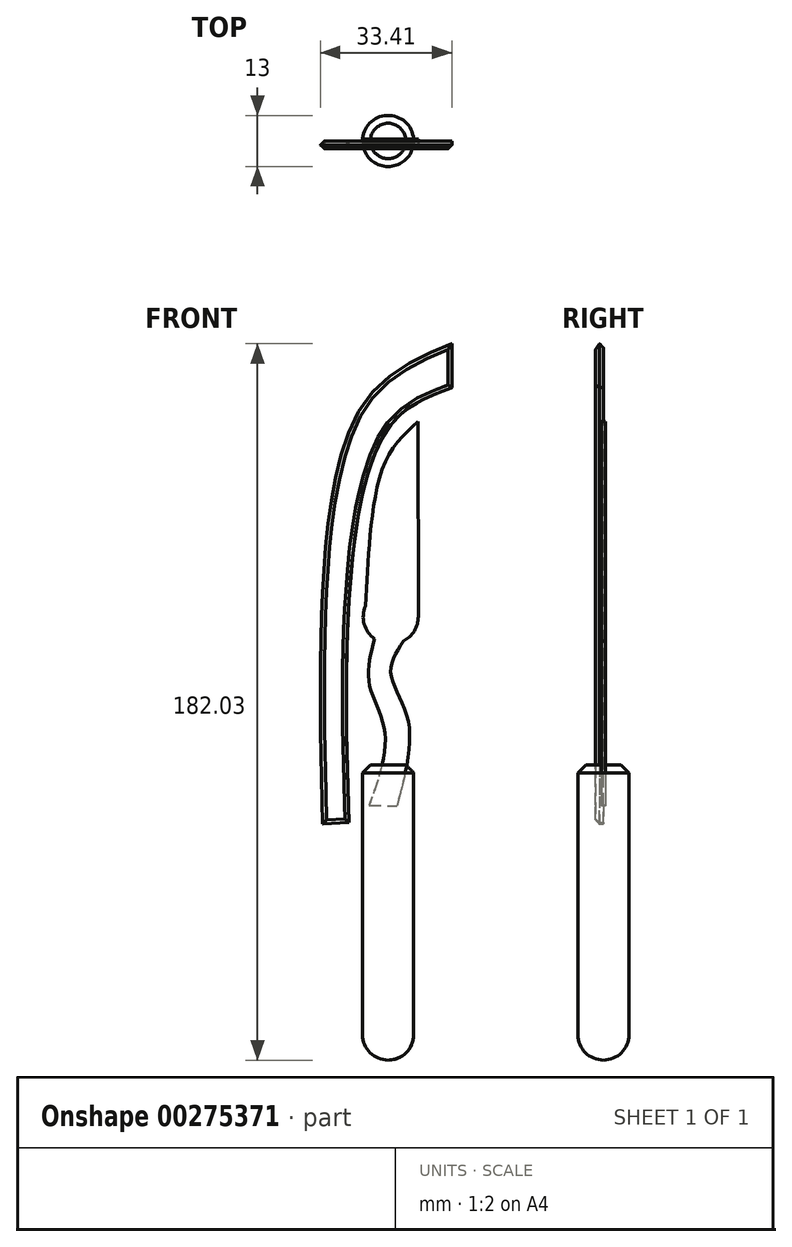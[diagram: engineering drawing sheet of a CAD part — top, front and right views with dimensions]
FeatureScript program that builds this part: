
annotation { "Feature Type Name" : "Feature", "Feature Type Description" : "" }
export const myFeature = defineFeature(function(context is Context, id is Id, definition is map)
    precondition{}
    {
        {
            var Q0;
            Q0=qCreatedBy(makeId("Front.planeOp"),FACE);
            var sketch = newSketch(context, id + "F0", { "sketchPlane" : qUnion([Q0])});
            skFitSpline(sketch, "E0", {"points": [v(-32.81, -75.03) * mm, v(-33.25, -28.22) * mm, v(-23.19, 30.63) * mm, v(0, 47.03) * mm], "startDerivative": vector(-3.63, 125.4) * mm, "endDerivative": vector(98.4, 40.35) * mm});
            skLineSegment(sketch, "E1", {"start": v(0, 47.03) * mm, "end": v(0, -72.97) * mm});
            skLineSegment(sketch, "E2", {"start": v(0, -72.97) * mm, "end": v(-32.81, -75.03) * mm});
            skFitSpline(sketch, "E3", {"points": [v(-26.07, -77.03) * mm, v(-26.63, -29.87) * mm, v(-15.47, 26.52) * mm, v(6.95, 38.95) * mm], "startDerivative": vector(-3.56, 125.4) * mm, "endDerivative": vector(93.73, 50.5) * mm});
            skLineSegment(sketch, "E4", {"start": v(-3.86, 34.35) * mm, "end": v(-3.86, -70.14) * mm});
            skLineSegment(sketch, "E5", {"start": v(-3.86, -70.14) * mm, "end": v(-26.28, -70.14) * mm});
            skSolve(sketch);
        }
        {
            var Q0;
            Q0=makeQuery(id+"F0.imprint","IMPRINT",FACE,{"disambiguationData":[TD([[makeQuery(id+"F0.imprint","IMPRINT",EDGE,{"derivedFrom":sQuery(id+"F0.wireOp",EDGE,"E0")}),-1.0]])]});
            extrude(context, id + "F1", {"entities" : qUnion([Q0]), "depth" : 2 * mm});
        }
        {
            var Q0;
            Q0=makeQuery(id+"F1.opExtrude","CAP_EDGE",EDGE,{"disambiguationData":[OSD([sQuery(id+"F0.wireOp",EDGE,"E0")])],"isStart":true});
            var Q1;
            Q1=makeQuery(id+"F1.opExtrude","CAP_FACE",FACE,{"disambiguationData":[OSD([sQuery(id+"F0.wireOp",EDGE,"E0"),sQuery(id+"F0.wireOp",EDGE,"E1"),sQuery(id+"F0.wireOp",EDGE,"E2")])],"isStart":false});
            chamfer(context, id + "F2", {"entities" : qUnion([Q0, Q1]), "width" : 1 * mm, "tangentPropagation" : true});
        }
        {
            var Q0;
            Q0=qCreatedBy(makeId("Front.planeOp"),FACE);
            var sketch = newSketch(context, id + "F3", { "sketchPlane" : qUnion([Q0])});
            skCircle(sketch, "E6", {"center": v(-15.53, -22.33) * mm, "radius": 7 * mm});
            skFitSpline(sketch, "E7", {"points": [v(-19.63, -28) * mm, v(-21, -39.4) * mm, v(-17.07, -51.43) * mm, v(-21, -70.25) * mm], "startDerivative": vector(-10.35, -38.65) * mm, "endDerivative": vector(-18.11, -51.63) * mm});
            skFitSpline(sketch, "E8", {"points": [v(-12.32, -28.55) * mm, v(-15.53, -36.55) * mm, v(-11.16, -48.59) * mm, v(-14, -70.47) * mm], "startDerivative": vector(-19.55, -29.62) * mm, "endDerivative": vector(-15.13, -56.02) * mm});
            skLineSegment(sketch, "E9", {"start": v(-21, -70.25) * mm, "end": v(-14, -70.47) * mm});
            skFitSpline(sketch, "E10", {"points": [v(-21.97, -19.58) * mm, v(-20.75, -1.57) * mm, v(-16.6, 17.77) * mm, v(-8.6, 27.2) * mm], "startDerivative": vector(2.68, 49.91) * mm, "endDerivative": vector(31.17, 27.84) * mm});
            skLineSegment(sketch, "E11", {"start": v(-8.6, 27.2) * mm, "end": v(-8.53, -22.32) * mm});
            skSolve(sketch);
        }
        {
            var Q0;
            {var subQ0=sQuery(id+"F3.wireOp",EDGE,"E6");var subQ1=makeQuery(id+"F3.imprint","INTERSECT",VERTEX,{"derivedFrom":[subQ0,sQuery(id+"F3.wireOp",EDGE,"E7")]});Q0=makeQuery(id+"F3.imprint","IMPRINT",FACE,{"disambiguationData":[TD([[makeQuery(id+"F3.imprint","IMPRINT",EDGE,{"disambiguationData":[TD([[subQ1,-1.0]])],"derivedFrom":subQ0}),1.0]])]});}
            var Q1;
            {var subQ0=sQuery(id+"F3.wireOp",EDGE,"E10");Q1=makeQuery(id+"F3.imprint","IMPRINT",FACE,{"disambiguationData":[TD([[makeQuery(id+"F3.imprint","IMPRINT",EDGE,{"derivedFrom":subQ0}),-1.0]])]});}
            var Q2;
            {var subQ0=sQuery(id+"F3.wireOp",EDGE,"E7");Q2=makeQuery(id+"F3.imprint","IMPRINT",FACE,{"disambiguationData":[TD([[makeQuery(id+"F3.imprint","IMPRINT",EDGE,{"derivedFrom":subQ0}),1.0]])]});}
            extrude(context, id + "F4", {"entities" : qUnion([Q0, Q1, Q2]), "endBound" : BoundingType.SYMMETRIC, "oppositeDirection" : true, "depth" : 1 * mm});
        }
        {
            var Q0;
            Q0=qCreatedBy(makeId("Top.planeOp"),FACE);
            cPlane(context, id + "F5", {"entities" : qUnion([Q0]), "cplaneType" : CPlaneType.OFFSET, "offset" : 60 * mm, "oppositeDirection" : true, "width" : 150 * mm, "height" : 150 * mm});
        }
        {
            var Q0;
            Q0=qCreatedBy(id+"F5.planeOp",FACE);
            var sketch = newSketch(context, id + "F6", { "sketchPlane" : qUnion([Q0])});
            skCircle(sketch, "E12", {"center": v(-16.2, 0) * mm, "radius": 6.5 * mm});
            skSolve(sketch);
        }
        {
            var Q0;
            Q0=makeQuery(id+"F6.imprint","IMPRINT",FACE,{"disambiguationData":[TD([[makeQuery(id+"F6.imprint","IMPRINT",EDGE,{"derivedFrom":sQuery(id+"F6.wireOp",EDGE,"E12")}),1.0]])]});
            extrude(context, id + "F7", {"entities" : qUnion([Q0]), "oppositeDirection" : true, "depth" : 75 * mm});
        }
        {
            var Q0;
            Q0=makeQuery(id+"F7.opExtrude","CAP_EDGE",EDGE,{"disambiguationData":[OSD([sQuery(id+"F6.wireOp",EDGE,"E12")])],"isStart":true});
            chamfer(context, id + "F8", {"entities" : qUnion([Q0]), "width" : 2 * mm, "tangentPropagation" : true});
        }
        {
            var Q0;
            Q0=makeQuery(id+"F7.opExtrude","CAP_EDGE",EDGE,{"disambiguationData":[OSD([sQuery(id+"F6.wireOp",EDGE,"E12")])],"isStart":false});
            fillet(context, id + "F9", {"entities" : qUnion([Q0]), "radius" : 6.5 * mm, "tangentPropagation" : true, "allowEdgeOverflow" : false});
        }
    });
